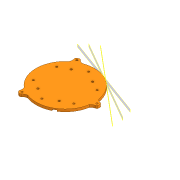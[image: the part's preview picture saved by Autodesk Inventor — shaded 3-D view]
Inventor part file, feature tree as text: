
AUTODESK INVENTOR PART (.ipt)
format: ipt  version: 2020.3 (Build 243373000, 373)  size: 324,608 bytes
history: native  units: mm
features: extrude x8, sketch x4, plane x3, fillet x2, pattern_circular x1
ambient origin geometry x8: Origin, YZ Plane, XZ Plane, XY Plane, X Axis, Y Axis, Z Axis, Center Point
bodies: Solid1 (feature_tree)
feature tree (18):
  sketch  "Sketch1"  dims[d0=95.0mm d1=120.0deg]
  extrude  "Extrusion1"  TaperAngle=120.0deg  [1 undecoded]
  plane  "Work Plane1"
  plane  "Work Plane2"
  plane  "Work Plane3"
  extrude  "Extrusion2"  Depth=16.0mm
  extrude  "Extrusion3"  Depth=6.0mm
  sketch  "Sketch2"  dims[d2=120.0deg d3=16.0mm]
  sketch  "Sketch3"  dims[d4=3.0mm d5=6.0mm]
  extrude  "Extrusion4"  Depth=10.0mm
  extrude  "Extrusion5"  Depth=10.0mm
  extrude  "Extrusion6"  Depth=10.0mm
  fillet  "Fillet1"  Radius=1.2mm
  fillet  "Fillet2"  Radius=4.0mm
  extrude  "Extrusion7"  Depth=10.0mm TaperAngle=360.0deg
  pattern_circular  "Circular Pattern1"  [2 undecoded]
  extrude  "Extrusion8"  Depth=10.0mm
  sketch  "Sketch4"  dims[d6=1.0mm d7=10.0mm d8=3.6mm d9=2.4mm d10=1.2mm d11=4.0mm d12=0.0mm d13=30.0mm d15=360.0deg d17=9.6mm d18=12.0mm d19=2.0mm d20=6.0mm d21=2.0mm d23=60.0deg d24=6.1mm d25=8.0mm d26=6.1mm d27=60.0deg d28=1.745329mm d29=1.745329mm d39=90.0deg d40=90.0deg d41=90.0deg d42=5.0mm d43=0.0mm d44=2.0mm d45=0.0mm d46=5.5mm d47=5.5mm d48=5.5mm d49=24.0mm d50=0.0mm d51=24.0mm d52=0.0mm d53=24.0mm d54=0.0mm d55=6.0mm d56=40.0mm d57=60.0mm d58=3.2mm d59=1.3mm d60=1.0mm d61=1.0mm d62=1.3mm d63=6.0mm d64=3.0mm d65=8.0mm d66=6.0mm d67=10.0mm d68=0.0mm d69=60.0mm d70=360.0deg d72=10.0mm d73=0.0mm d74=0.5mm d75=0.872665mm d76=0.5mm d77=0.872665mm]
note: 3 required parameter values undecoded (feature->parameter linkage not recoverable at this tier; creation-order binding heuristic only, values carry confidence <= 0.55)
